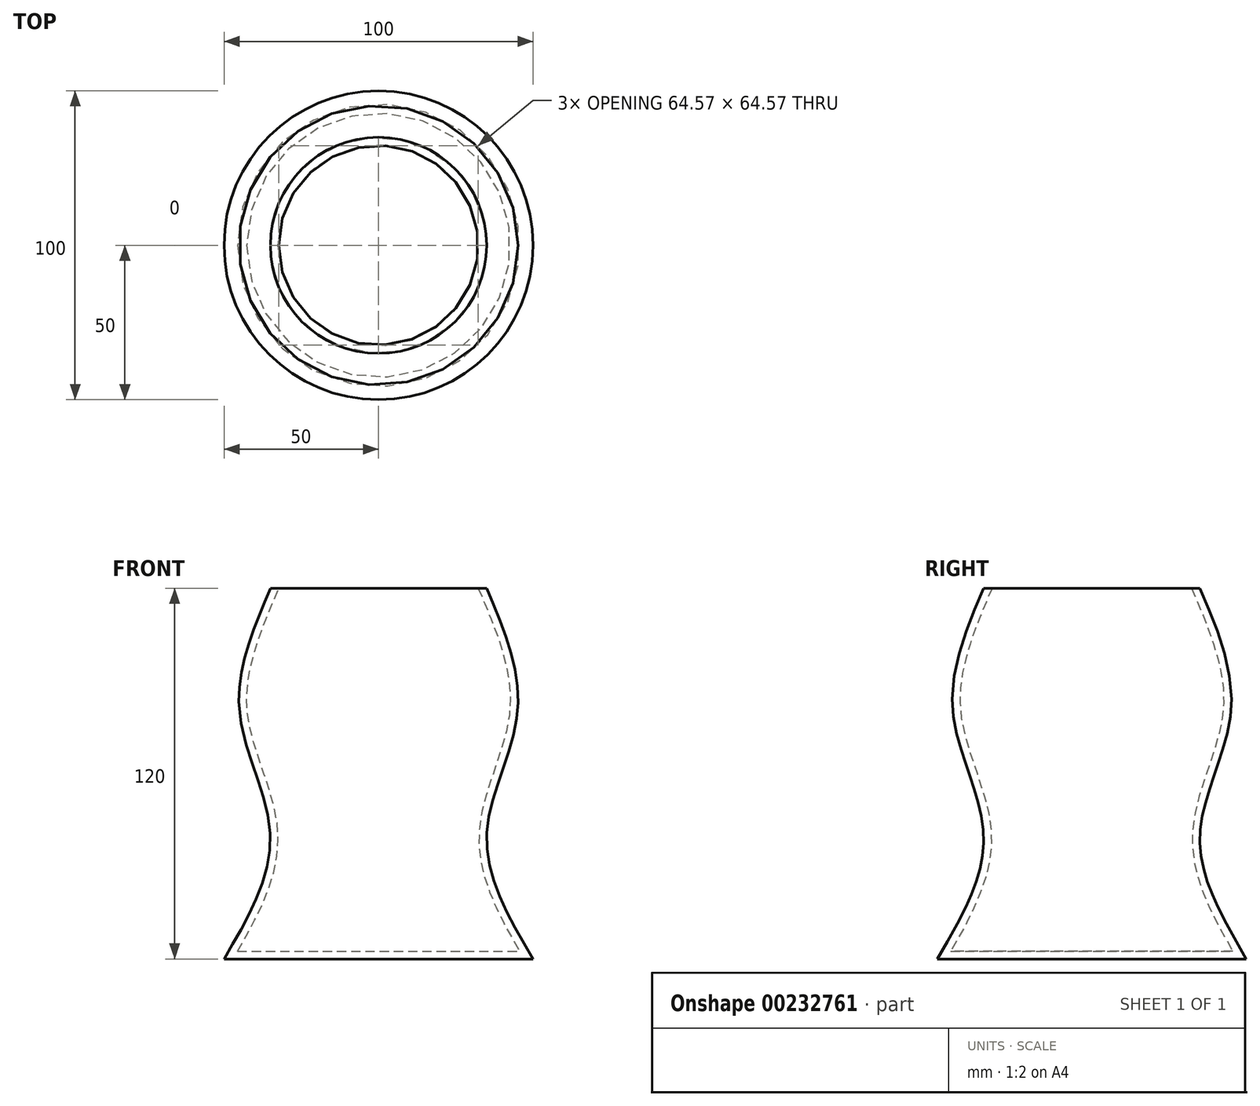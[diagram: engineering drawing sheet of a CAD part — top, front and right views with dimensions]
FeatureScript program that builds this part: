
annotation { "Feature Type Name" : "Feature", "Feature Type Description" : "" }
export const myFeature = defineFeature(function(context is Context, id is Id, definition is map)
    precondition{}
    {
        {
            var Q0;
            Q0=qCreatedBy(makeId("Top.planeOp"),FACE);
            var sketch = newSketch(context, id + "F0", { "sketchPlane" : qUnion([Q0])});
            skCircle(sketch, "E0", {"center": v(0, 0) * mm, "radius": 50 * mm});
            skSolve(sketch);
        }
        {
            var Q0;
            Q0=qCreatedBy(makeId("Top.planeOp"),FACE);
            cPlane(context, id + "F1", {"entities" : qUnion([Q0]), "cplaneType" : CPlaneType.OFFSET, "offset" : 40 * mm, "width" : 150 * mm, "height" : 150 * mm});
        }
        {
            var Q0;
            Q0=qCreatedBy(id+"F1.planeOp",FACE);
            var sketch = newSketch(context, id + "F2", { "sketchPlane" : qUnion([Q0])});
            skCircle(sketch, "E1", {"center": v(0, 0) * mm, "radius": 35 * mm});
            skSolve(sketch);
        }
        {
            var Q0;
            Q0=qCreatedBy(id+"F1.planeOp",FACE);
            cPlane(context, id + "F3", {"entities" : qUnion([Q0]), "cplaneType" : CPlaneType.OFFSET, "offset" : 40 * mm, "width" : 150 * mm, "height" : 150 * mm});
        }
        {
            var Q0;
            Q0=qCreatedBy(id+"F3.planeOp",FACE);
            var sketch = newSketch(context, id + "F4", { "sketchPlane" : qUnion([Q0])});
            skCircle(sketch, "E2", {"center": v(0, 0) * mm, "radius": 45 * mm});
            skSolve(sketch);
        }
        {
            var Q0;
            Q0=qCreatedBy(id+"F3.planeOp",FACE);
            cPlane(context, id + "F5", {"entities" : qUnion([Q0]), "cplaneType" : CPlaneType.OFFSET, "offset" : 40 * mm, "width" : 150 * mm, "height" : 150 * mm});
        }
        {
            var Q0;
            Q0=qCreatedBy(id+"F5.planeOp",FACE);
            var sketch = newSketch(context, id + "F6", { "sketchPlane" : qUnion([Q0])});
            skCircle(sketch, "E3", {"center": v(0, 0) * mm, "radius": 35 * mm});
            skSolve(sketch);
        }
        {
            var Q0;
            Q0=makeQuery(id+"F0.imprint","IMPRINT",FACE,{"disambiguationData":[TD([[makeQuery(id+"F0.imprint","IMPRINT",EDGE,{"derivedFrom":sQuery(id+"F0.wireOp",EDGE,"E0")}),1.0]])]});
            var Q1;
            Q1=makeQuery(id+"F2.imprint","IMPRINT",FACE,{"disambiguationData":[TD([[makeQuery(id+"F2.imprint","IMPRINT",EDGE,{"derivedFrom":sQuery(id+"F2.wireOp",EDGE,"E1")}),1.0]])]});
            var Q2;
            Q2=makeQuery(id+"F4.imprint","IMPRINT",FACE,{"disambiguationData":[TD([[makeQuery(id+"F4.imprint","IMPRINT",EDGE,{"derivedFrom":sQuery(id+"F4.wireOp",EDGE,"E2")}),1.0]])]});
            var Q3;
            Q3=makeQuery(id+"F6.imprint","IMPRINT",FACE,{"disambiguationData":[TD([[makeQuery(id+"F6.imprint","IMPRINT",EDGE,{"derivedFrom":sQuery(id+"F6.wireOp",EDGE,"E3")}),1.0]])]});
            loft(context, id + "F7", {"sheetProfilesArray" : [{ "sheetProfileEntities" : qUnion([Q0]) }, { "sheetProfileEntities" : qUnion([Q1]) }, { "sheetProfileEntities" : qUnion([Q2]) }, { "sheetProfileEntities" : qUnion([Q3]) }]});
        }
        {
            var Q0;
            Q0=makeQuery(id+"F7.opLoft","CAP_FACE",FACE,{"disambiguationData":[OSD([makeQuery(id+"F6.imprint","IMPRINT",FACE,{"disambiguationData":[TD([[makeQuery(id+"F6.imprint","IMPRINT",EDGE,{"derivedFrom":sQuery(id+"F6.wireOp",EDGE,"E3")}),1.0]])]})])],"isStart":true});
            shell(context, id + "F8", {"entities" : qUnion([Q0]), "thickness" : 2.5 * mm});
        }
    });
